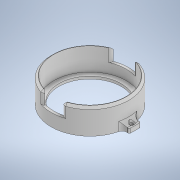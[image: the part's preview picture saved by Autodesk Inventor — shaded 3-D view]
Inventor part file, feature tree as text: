
AUTODESK INVENTOR PART (.ipt)
format: ipt  version: 2022 (Build 260153000, 153)  size: 264,704 bytes
history: native  units: in
note: dims shown in document units (in); Inventor stores cm internally (conversion verified against a paired STEP export)
features: sketch x6, extrude x4, fillet x3, pattern_circular x2, chamfer x2, revolve x1, hole x1
ambient origin geometry x8: Origin, YZ Plane, XZ Plane, XY Plane, X Axis, Y Axis, Z Axis, Center Point
bodies: Solid1 (feature_tree)
feature tree (19):
  extrude  "Extrusion1"  Depth=0.7874in TaperAngle=0.0deg
  extrude  "Extrusion2"  Depth=0.7087in TaperAngle=0.0deg
  extrude  "Extrusion3"  Depth=0.0787in TaperAngle=0.0deg
  extrude  "Extrusion4"  Depth=0.6299in
  pattern_circular  "Circular Pattern1"  [2 undecoded]
  fillet  "Fillet1"  Radius=0.7874in
  chamfer  "Chamfer3"  Distance=0.0787in
  revolve  "Revolution2"  Angle=45.0deg
  fillet  "Fillet9"  Radius=0.1969in
  fillet  "Fillet10"  Radius=0.1378in
  hole  "Hole2"  [1 undecoded]
  chamfer  "Chamfer5"  Distance=0.1378in
  pattern_circular  "Circular Pattern3"  [2 undecoded]
  sketch  "Sketch1"  dims[d0=2.4252in d1=0.7874in d2=0.0in]
  sketch  "Sketch2"  dims[d3=2.2677in d4=0.7087in d5=0.0in]
  sketch  "Sketch3"  dims[d6=1.9528in d7=0.0787in d8=0.0in]
  sketch  "Sketch4"  dims[d9=0.0in d10=0.6299in]
  sketch  "Sketch8"  dims[d11=60.0deg]
  sketch  "Sketch9"  dims[d12=120.0deg d13=0.3937in d14=0.0in d15=0.7874in d16=360.0deg d18=0.0787in d54=0.0669in d55=0.0787in d56=45.0deg d65=0.1969in d66=0.1378in d67=15.0deg d68=0.1378in d69=0.0394in d70=1.2992in d71=0.0984in d72=0.2362in d73=0.1575in d74=0.0787in d75=90.0deg d76=0.315in d77=0.8108in d78=0.0315in d79=0.0787in d80=45.0deg d81=0.7874in d82=360.0deg d84=0.0197in d85=0.0344in d86=0.0197in d87=0.0344in]
note: 5 required parameter values undecoded (feature->parameter linkage not recoverable at this tier; creation-order binding heuristic only, values carry confidence <= 0.55)
